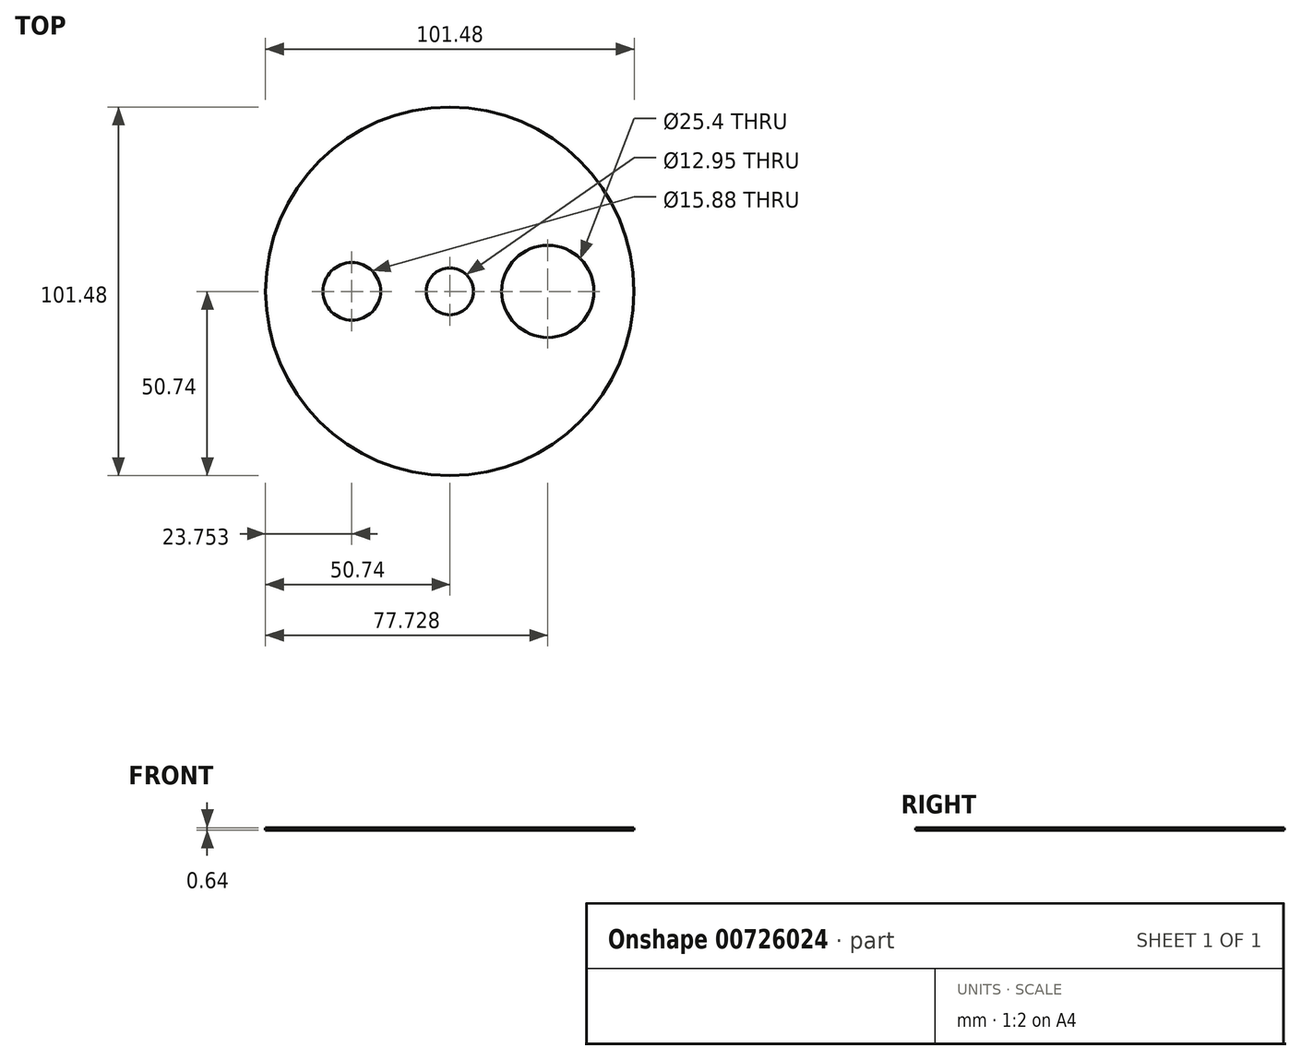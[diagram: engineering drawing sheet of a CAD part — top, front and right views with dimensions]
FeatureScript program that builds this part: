
annotation { "Feature Type Name" : "Feature", "Feature Type Description" : "" }
export const myFeature = defineFeature(function(context is Context, id is Id, definition is map)
    precondition{}
    {
        {
            var Q0;
            Q0=qCreatedBy(makeId("Top.planeOp"),FACE);
            var sketch = newSketch(context, id + "F0", { "sketchPlane" : qUnion([Q0])});
            skCircle(sketch, "E0", {"center": v(0, 0) * mm, "radius": 50.74 * mm});
            skCircle(sketch, "E1", {"center": v(0, 0) * mm, "radius": 6.48 * mm});
            skCircle(sketch, "E2", {"center": v(0, 0) * mm, "radius": 26.99 * mm, "construction": true});
            skCircle(sketch, "E3", {"center": v(26.99, 0) * mm, "radius": 12.7 * mm});
            skCircle(sketch, "E4", {"center": v(0, 0) * mm, "radius": 44.45 * mm});
            skCircle(sketch, "E5", {"center": v(-26.99, 0) * mm, "radius": 7.94 * mm});
            skSolve(sketch);
        }
        {
            var Q0;
            Q0=makeQuery(id+"F0.imprint","IMPRINT",FACE,{"disambiguationData":[TD([[makeQuery(id+"F0.imprint","IMPRINT",EDGE,{"derivedFrom":sQuery(id+"F0.wireOp",EDGE,"E0")}),1.0]])]});
            var Q1;
            Q1=makeQuery(id+"F0.imprint","IMPRINT",FACE,{"disambiguationData":[TD([[makeQuery(id+"F0.imprint","IMPRINT",EDGE,{"derivedFrom":sQuery(id+"F0.wireOp",EDGE,"E1")}),-1.0]])]});
            extrude(context, id + "F1", {"entities" : qUnion([Q0, Q1]), "oppositeDirection" : true, "depth" : 0.64 * mm, "offsetDistance" : 25.4 * mm});
        }
    });
